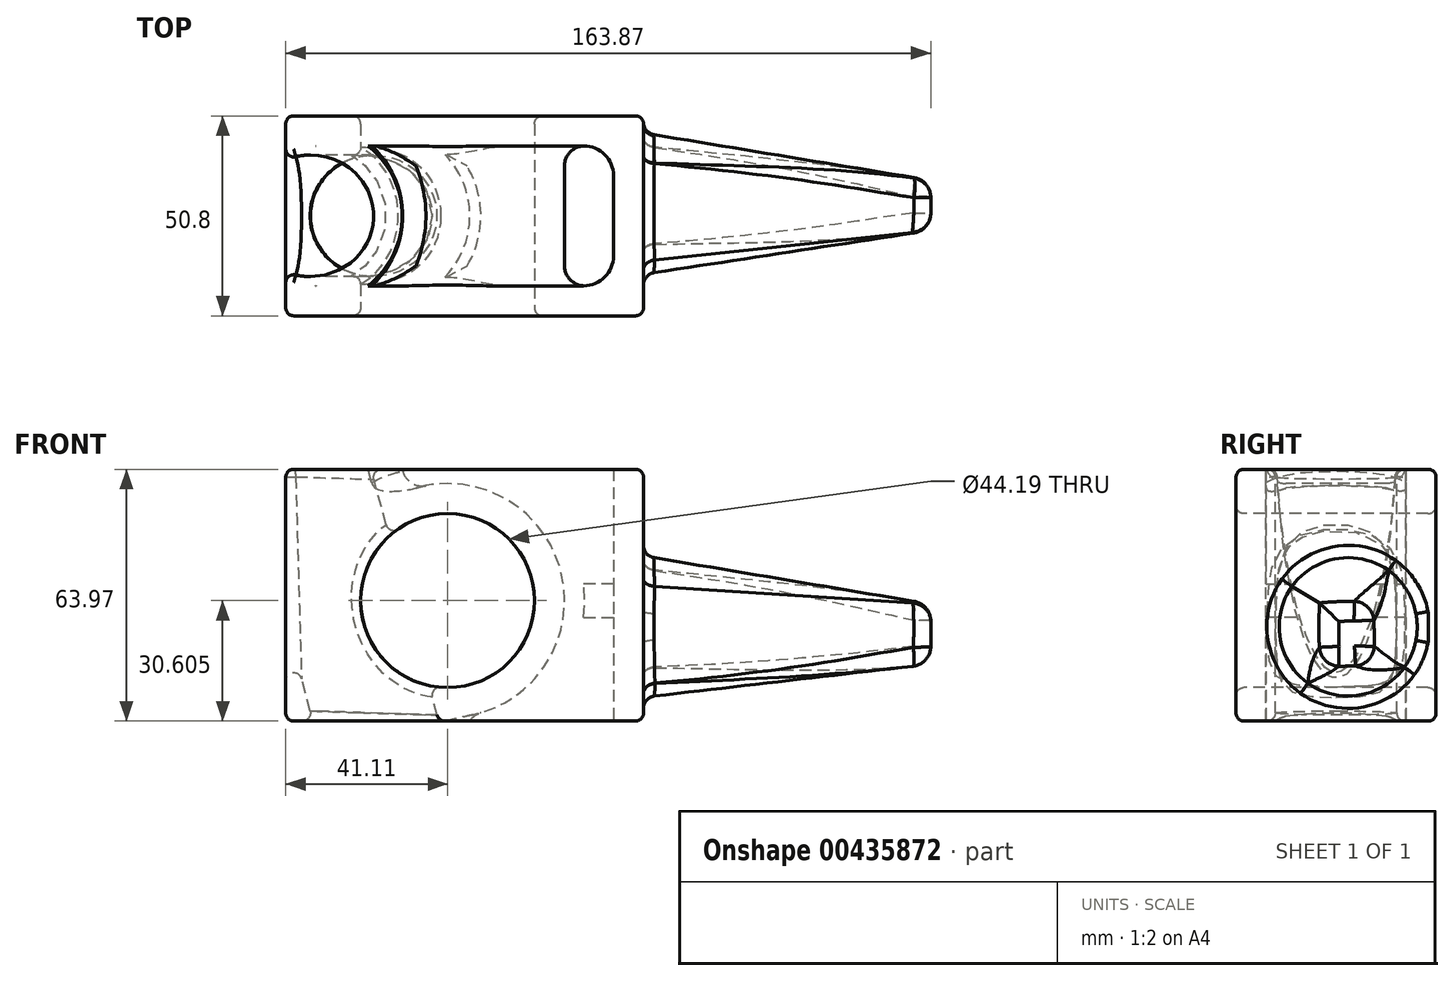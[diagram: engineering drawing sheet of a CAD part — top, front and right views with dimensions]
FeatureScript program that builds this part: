
annotation { "Feature Type Name" : "Feature", "Feature Type Description" : "" }
export const myFeature = defineFeature(function(context is Context, id is Id, definition is map)
    precondition{}
    {
        {
            var Q0;
            Q0=qCreatedBy(makeId("Front.planeOp"),FACE);
            var sketch = newSketch(context, id + "F0", { "sketchPlane" : qUnion([Q0])});
            skLineSegment(sketch, "E0.bottom", {"start": v(-36.87, 43.32) * mm, "end": v(54.02, 43.32) * mm});
            skLineSegment(sketch, "E0.top", {"start": v(-36.87, -20.65) * mm, "end": v(54.02, -20.65) * mm});
            skLineSegment(sketch, "E0.left", {"start": v(-36.87, 43.32) * mm, "end": v(-36.87, -20.65) * mm});
            skLineSegment(sketch, "E0.right", {"start": v(54.02, 43.32) * mm, "end": v(54.02, -20.65) * mm});
            skSolve(sketch);
        }
        {
            var Q0;
            Q0 = qSketchRegion(id + "F0", true);
            extrude(context, id + "F1", {"entities" : qUnion([Q0]), "depth" : 50.8 * mm});
        }
        {
            var Q0;
            Q0=makeQuery(id+"F1.opExtrude","CAP_FACE",FACE,{"disambiguationData":[OSD([sQuery(id+"F0.wireOp",EDGE,"E0.bottom"),sQuery(id+"F0.wireOp",EDGE,"E0.top"),sQuery(id+"F0.wireOp",EDGE,"E0.left"),sQuery(id+"F0.wireOp",EDGE,"E0.right")])],"isStart":false});
            var sketch = newSketch(context, id + "F2", { "sketchPlane" : qUnion([Q0])});
            skCircle(sketch, "E1", {"center": v(4.24, 9.96) * mm, "radius": 22.1 * mm});
            skSolve(sketch);
        }
        {
            var Q0;
            Q0 = qSketchRegion(id + "F2", true);
            extrude(context, id + "F3", {"entities" : qUnion([Q0]), "operationType" : NewBodyOperationType.REMOVE, "endBound" : BoundingType.THROUGH_ALL, "oppositeDirection" : true, "depth" : 25.4 * mm});
        }
        {
            var Q0;
            Q0=qCreatedBy(makeId("Top.planeOp"),FACE);
            var Q1;
            Q1=makeQuery(id+"F1.opExtrude","SWEPT_EDGE",EDGE,{"disambiguationData":[OSD([sQuery(id+"F0.wireOp",EDGE,"E0.bottom"),sQuery(id+"F0.wireOp",EDGE,"E0.left")])]});
            cPlane(context, id + "F4", {"entities" : qUnion([Q0, Q1]), "cplaneType" : CPlaneType.LINE_ANGLE, "offset" : 25.4 * mm, "angle" : 15 * degree, "oppositeDirection" : true, "width" : 152.4 * mm, "height" : 152.4 * mm});
        }
        {
            var Q0;
            Q0=qCreatedBy(id+"F4.planeOp",FACE);
            var sketch = newSketch(context, id + "F5", { "sketchPlane" : qUnion([Q0])});
            skCircle(sketch, "E2", {"center": v(-18.87, 25.4) * mm, "radius": 15.45 * mm});
            skSolve(sketch);
        }
        {
            var Q0;
            Q0 = qSketchRegion(id + "F5", true);
            extrude(context, id + "F6", {"entities" : qUnion([Q0]), "operationType" : NewBodyOperationType.REMOVE, "endBound" : BoundingType.THROUGH_ALL, "depth" : 25.4 * mm});
        }
        {
            var Q0;
            Q0=makeQuery(id+"F1.opExtrude","SWEPT_FACE",FACE,{"disambiguationData":[OSD([sQuery(id+"F0.wireOp",EDGE,"E0.bottom")])]});
            var Q1;
            Q1=makeQuery(id+"F1.opExtrude","CAP_FACE",FACE,{"disambiguationData":[OSD([sQuery(id+"F0.wireOp",EDGE,"E0.bottom"),sQuery(id+"F0.wireOp",EDGE,"E0.top"),sQuery(id+"F0.wireOp",EDGE,"E0.left"),sQuery(id+"F0.wireOp",EDGE,"E0.right")])],"isStart":false});
            var Q2;
            Q2=makeQuery(id+"F1.opExtrude","CAP_FACE",FACE,{"disambiguationData":[OSD([sQuery(id+"F0.wireOp",EDGE,"E0.bottom"),sQuery(id+"F0.wireOp",EDGE,"E0.top"),sQuery(id+"F0.wireOp",EDGE,"E0.left"),sQuery(id+"F0.wireOp",EDGE,"E0.right")])],"isStart":true});
            var Q3;
            Q3=makeQuery(id+"F1.opExtrude","SWEPT_FACE",FACE,{"disambiguationData":[OSD([sQuery(id+"F0.wireOp",EDGE,"E0.right")])]});
            var Q4;
            Q4=makeQuery(id+"F1.opExtrude","SWEPT_FACE",FACE,{"disambiguationData":[OSD([sQuery(id+"F0.wireOp",EDGE,"E0.top")])]});
            var Q5;
            Q5=makeQuery(id+"F1.opExtrude","SWEPT_EDGE",EDGE,{"disambiguationData":[OSD([sQuery(id+"F0.wireOp",EDGE,"E0.top"),sQuery(id+"F0.wireOp",EDGE,"E0.left")])]});
            var Q6;
            Q6=makeQuery(id+"F1.opExtrude","SWEPT_FACE",FACE,{"disambiguationData":[OSD([sQuery(id+"F0.wireOp",EDGE,"E0.left")])]});
            var Q7;
            Q7=makeQuery(id+"F3.boolean.opBoolean","COPY",FACE,{"derivedFrom":makeQuery(id+"F3.opExtrude","SWEPT_FACE",FACE,{"disambiguationData":[OSD([sQuery(id+"F2.wireOp",EDGE,"E1")])]})});
            fillet(context, id + "F7", {"entities" : qUnion([Q0, Q1, Q2, Q3, Q4, Q5, Q6, Q7]), "radius" : 2.03 * mm, "tangentPropagation" : true, "allowEdgeOverflow" : false});
        }
        {
            var Q0;
            Q0=makeQuery(id+"F1.opExtrude","SWEPT_FACE",FACE,{"disambiguationData":[OSD([sQuery(id+"F0.wireOp",EDGE,"E0.top")])]});
            var Q1;
            Q1=makeQuery(id+"F1.opExtrude","SWEPT_FACE",FACE,{"disambiguationData":[OSD([sQuery(id+"F0.wireOp",EDGE,"E0.bottom")])]});
            shell(context, id + "F8", {"entities" : qUnion([Q0, Q1]), "thickness" : 7.62 * mm});
        }
        {
            var Q0;
            Q0=makeQuery(id+"F8.opShell","OFFSET_FACE",FACE,{"disambiguationData":[OSD([sQuery(id+"F2.wireOp",EDGE,"E1")])]});
            fillet(context, id + "F9", {"entities" : qUnion([Q0]), "radius" : 5.08 * mm, "tangentPropagation" : true, "allowEdgeOverflow" : false});
        }
        {
            var Q0;
            {var subQ0=sQuery(id+"F0.wireOp",EDGE,"E0.right");var subQ1=sQuery(id+"F0.wireOp",EDGE,"E0.left");var subQ2=sQuery(id+"F0.wireOp",EDGE,"E0.top");var subQ3=sQuery(id+"F0.wireOp",EDGE,"E0.bottom");var subQ4=makeQuery(id+"F1.opExtrude","CAP_EDGE",EDGE,{"disambiguationData":[OSD([subQ0])],"isStart":false});Q0=makeQuery(id+"F8.opShell","OFFSET_EDGE",EDGE,{"disambiguationData":[OSD([subQ3,subQ2,subQ1,subQ0]),TDD([makeQuery(id+"F7.opFillet","BLEND_EDGE",EDGE,{"blendedFrom":[subQ4,makeQuery(id+"F1.opExtrude","SWEPT_FACE",FACE,{"disambiguationData":[OSD([subQ0])]})],"blendedInto":[makeQuery(id+"F1.opExtrude","SWEPT_FACE",FACE,{"disambiguationData":[OSD([subQ0])]})]}),makeQuery(id+"F7.opFillet","BLEND_EDGE",EDGE,{"blendedFrom":[subQ4,makeQuery(id+"F1.opExtrude","CAP_FACE",FACE,{"disambiguationData":[OSD([subQ3,subQ2,subQ1,subQ0])],"isStart":false})],"blendedInto":[makeQuery(id+"F1.opExtrude","CAP_FACE",FACE,{"disambiguationData":[OSD([subQ3,subQ2,subQ1,subQ0])],"isStart":false})]})])]});}
            var Q1;
            {var subQ0=sQuery(id+"F0.wireOp",EDGE,"E0.right");var subQ1=sQuery(id+"F0.wireOp",EDGE,"E0.left");var subQ2=sQuery(id+"F0.wireOp",EDGE,"E0.top");var subQ3=sQuery(id+"F0.wireOp",EDGE,"E0.bottom");var subQ4=makeQuery(id+"F1.opExtrude","CAP_EDGE",EDGE,{"disambiguationData":[OSD([subQ0])],"isStart":true});Q1=makeQuery(id+"F8.opShell","OFFSET_EDGE",EDGE,{"disambiguationData":[OSD([subQ3,subQ2,subQ1,subQ0]),TDD([makeQuery(id+"F7.opFillet","BLEND_EDGE",EDGE,{"blendedFrom":[subQ4,makeQuery(id+"F1.opExtrude","SWEPT_FACE",FACE,{"disambiguationData":[OSD([subQ0])]})],"blendedInto":[makeQuery(id+"F1.opExtrude","SWEPT_FACE",FACE,{"disambiguationData":[OSD([subQ0])]})]}),makeQuery(id+"F7.opFillet","BLEND_EDGE",EDGE,{"blendedFrom":[subQ4,makeQuery(id+"F1.opExtrude","CAP_FACE",FACE,{"disambiguationData":[OSD([subQ3,subQ2,subQ1,subQ0])],"isStart":true})],"blendedInto":[makeQuery(id+"F1.opExtrude","CAP_FACE",FACE,{"disambiguationData":[OSD([subQ3,subQ2,subQ1,subQ0])],"isStart":true})]})])]});}
            fillet(context, id + "F10", {"entities" : qUnion([Q0, Q1]), "radius" : 7.62 * mm, "tangentPropagation" : true, "allowEdgeOverflow" : false});
        }
        {
            var Q0;
            Q0=makeQuery(id+"F1.opExtrude","SWEPT_FACE",FACE,{"disambiguationData":[OSD([sQuery(id+"F0.wireOp",EDGE,"E0.right")])]});
            var sketch = newSketch(context, id + "F11", { "sketchPlane" : qUnion([Q0])});
            skCircle(sketch, "E3", {"center": v(-22.3, 3.35) * mm, "radius": 17.95 * mm});
            skSolve(sketch);
        }
        {
            var Q0;
            Q0=qCreatedBy(makeId("Right.planeOp"),FACE);
            cPlane(context, id + "F12", {"entities" : qUnion([Q0]), "cplaneType" : CPlaneType.OFFSET, "offset" : 127 * mm, "width" : 152.4 * mm, "height" : 152.4 * mm});
        }
        {
            var Q0;
            Q0=qCreatedBy(id+"F12.planeOp",FACE);
            var sketch = newSketch(context, id + "F13", { "sketchPlane" : qUnion([Q0])});
            skLineSegment(sketch, "E4.bottom", {"start": v(-29.1, -6.2) * mm, "end": v(-16.4, -6.2) * mm});
            skLineSegment(sketch, "E4.top", {"start": v(-29.1, 9.05) * mm, "end": v(-16.4, 9.05) * mm});
            skLineSegment(sketch, "E4.left", {"start": v(-29.1, -6.2) * mm, "end": v(-29.1, 9.05) * mm});
            skLineSegment(sketch, "E4.right", {"start": v(-16.4, -6.2) * mm, "end": v(-16.4, 9.05) * mm});
            skSolve(sketch);
        }
        {
            var Q1;
            Q1 = qSketchRegion(id + "F13", true);
            var Q2;
            Q2 = qSketchRegion(id + "F11", true);
            loft(context, id + "F14", {"operationType" : NewBodyOperationType.ADD, "sheetProfilesArray" : [{ "sheetProfileEntities" : qUnion([Q1]) }, { "sheetProfileEntities" : qUnion([Q2]) }]});
        }
        {
            var Q0;
            Q0=makeQuery(id+"F1.opExtrude","SWEPT_FACE",FACE,{"disambiguationData":[OSD([sQuery(id+"F0.wireOp",EDGE,"E0.right")])]});
            fillet(context, id + "F15", {"entities" : qUnion([Q0]), "radius" : 3.17 * mm, "tangentPropagation" : true, "allowEdgeOverflow" : false});
        }
        {
            var Q0;
            Q0=makeQuery(id+"F14.opLoft","CAP_FACE",FACE,{"disambiguationData":[OSD([makeQuery(id+"F13.imprint","IMPRINT",FACE,{"disambiguationData":[TD([[makeQuery(id+"F13.imprint","IMPRINT",EDGE,{"derivedFrom":sQuery(id+"F13.wireOp",EDGE,"E4.bottom")}),1.0]])]})])],"isStart":true});
            var Q1;
            Q1=makeQuery(id+"F14.opLoft","SWEPT_EDGE",EDGE,{"disambiguationData":[OSD([sQuery(id+"F11.wireOp",EDGE,"E3"),sQuery(id+"F13.wireOp",EDGE,"E4.bottom"),sQuery(id+"F13.wireOp",EDGE,"E4.top"),sQuery(id+"F13.wireOp",EDGE,"E4.left")])]});
            var Q2;
            Q2=makeQuery(id+"F14.opLoft","SWEPT_EDGE",EDGE,{"disambiguationData":[OSD([sQuery(id+"F13.wireOp",EDGE,"E4.bottom"),sQuery(id+"F13.wireOp",EDGE,"E4.left")])]});
            var Q3;
            Q3=makeQuery(id+"F14.opLoft","SWEPT_EDGE",EDGE,{"disambiguationData":[OSD([sQuery(id+"F11.wireOp",EDGE,"E3"),sQuery(id+"F13.wireOp",EDGE,"E4.bottom"),sQuery(id+"F13.wireOp",EDGE,"E4.top"),sQuery(id+"F13.wireOp",EDGE,"E4.right")])]});
            var Q4;
            Q4=makeQuery(id+"F14.opLoft","SWEPT_EDGE",EDGE,{"disambiguationData":[OSD([sQuery(id+"F11.wireOp",EDGE,"E3"),sQuery(id+"F13.wireOp",EDGE,"E4.top"),sQuery(id+"F13.wireOp",EDGE,"E4.left"),sQuery(id+"F13.wireOp",EDGE,"E4.right")])]});
            fillet(context, id + "F16", {"entities" : qUnion([Q0, Q1, Q2, Q3, Q4]), "radius" : 5.08 * mm, "tangentPropagation" : true, "allowEdgeOverflow" : false});
        }
    });
